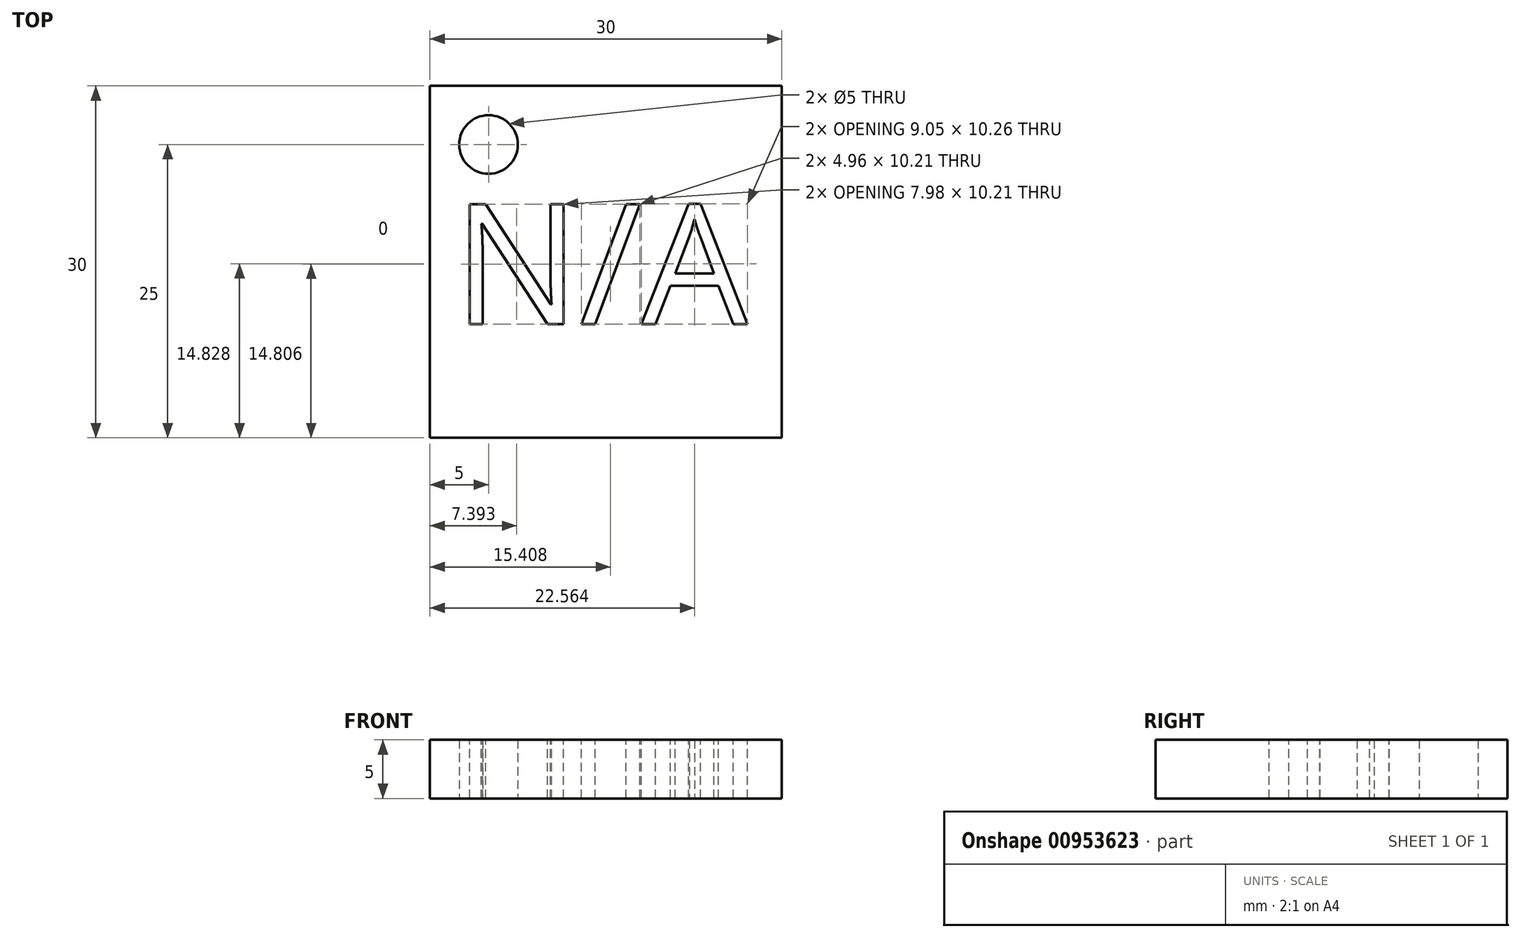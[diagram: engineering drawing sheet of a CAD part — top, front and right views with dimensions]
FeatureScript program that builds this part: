
annotation { "Feature Type Name" : "Feature", "Feature Type Description" : "" }
export const myFeature = defineFeature(function(context is Context, id is Id, definition is map)
    precondition{}
    {
        {
            var Q0;
            Q0=qCreatedBy(makeId("Top.planeOp"),FACE);
            var sketch = newSketch(context, id + "F0", { "sketchPlane" : qUnion([Q0])});
            skLineSegment(sketch, "E0.bottom", {"start": v(0, 0) * mm, "end": v(30, 0) * mm});
            skLineSegment(sketch, "E0.top", {"start": v(0, 30) * mm, "end": v(30, 30) * mm});
            skLineSegment(sketch, "E0.left", {"start": v(0, 0) * mm, "end": v(0, 30) * mm});
            skLineSegment(sketch, "E0.right", {"start": v(30, 0) * mm, "end": v(30, 30) * mm});
            skCircle(sketch, "E1", {"center": v(5, 25) * mm, "radius": 2.5 * mm});
            skSolve(sketch);
        }
        {
            var Q0;
            Q0=makeQuery(id+"F0.imprint","IMPRINT",FACE,{"disambiguationData":[TD([[makeQuery(id+"F0.imprint","IMPRINT",EDGE,{"derivedFrom":sQuery(id+"F0.wireOp",EDGE,"E0.bottom")}),1.0]])]});
            extrude(context, id + "F1", {"entities" : qUnion([Q0]), "depth" : 5 * mm, "offsetDistance" : 25 * mm});
        }
        {
            var Q0;
            Q0=makeQuery(id+"F1.opExtrude","CAP_FACE",FACE,{"disambiguationData":[OSD([sQuery(id+"F0.wireOp",EDGE,"E0.bottom"),sQuery(id+"F0.wireOp",EDGE,"E0.top"),sQuery(id+"F0.wireOp",EDGE,"E0.left"),sQuery(id+"F0.wireOp",EDGE,"E0.right"),sQuery(id+"F0.wireOp",EDGE,"E1")])],"isStart":false});
            var sketch = newSketch(context, id + "F2", { "sketchPlane" : qUnion([Q0])});
            skText(sketch, "E2", { "text": "N/A", "fontName": "OpenSans-Regular.ttf"});
            const initialGuessF2  = {"E2": [0.002, 0.0097, 1, 0, 0.0103]};
            skSetInitialGuess(sketch, initialGuessF2);
            skSolve(sketch);
        }
        {
            var Q0;
            Q0 = qSketchRegion(id + "F2", true);
            extrude(context, id + "F3", {"entities" : qUnion([Q0]), "operationType" : NewBodyOperationType.REMOVE, "endBound" : BoundingType.THROUGH_ALL, "oppositeDirection" : true, "depth" : 25 * mm, "offsetDistance" : 25 * mm});
        }
    });
